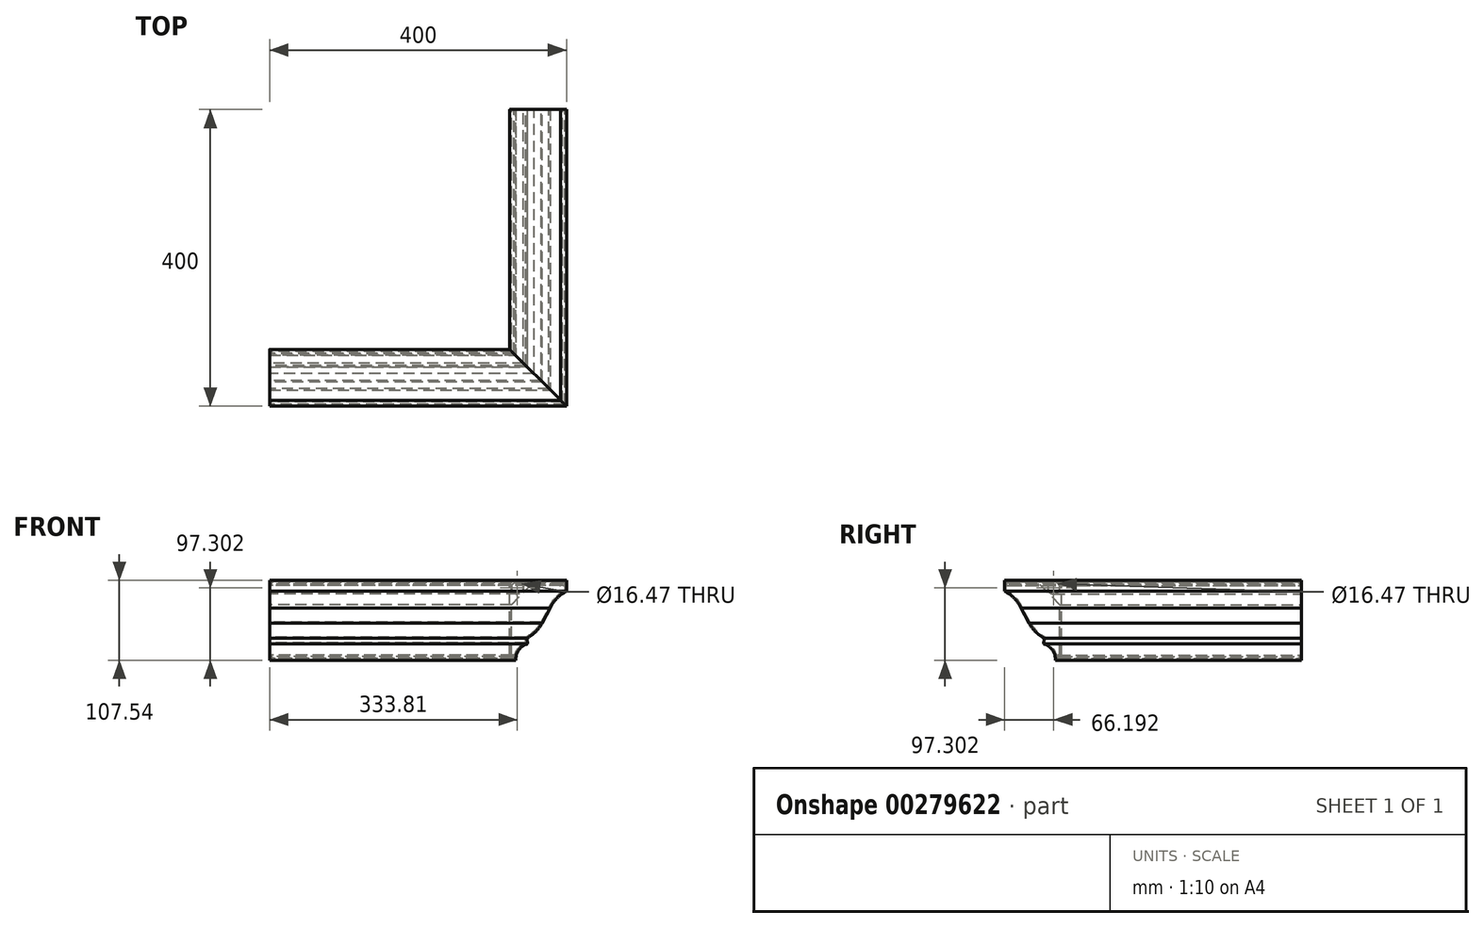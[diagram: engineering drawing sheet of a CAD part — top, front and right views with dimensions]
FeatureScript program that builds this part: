
annotation { "Feature Type Name" : "Feature", "Feature Type Description" : "" }
export const myFeature = defineFeature(function(context is Context, id is Id, definition is map)
    precondition{}
    {
        {
            var Q0;
            Q0=qCreatedBy(makeId("Front.planeOp"),FACE);
            var sketch = newSketch(context, id + "F0", { "sketchPlane" : qUnion([Q0])});
            skLineSegment(sketch, "E0", {"start": v(8.47, 2.23) * mm, "end": v(6.97, 0.18) * mm});
            skLineSegment(sketch, "E1", {"start": v(6.97, 0.18) * mm, "end": v(6.8, 0.14) * mm});
            skLineSegment(sketch, "E2", {"start": v(8.76, 2.82) * mm, "end": v(8.46, 2.4) * mm});
            skLineSegment(sketch, "E3", {"start": v(8.47, 2.23) * mm, "end": v(8.46, 2.4) * mm});
            skLineSegment(sketch, "E4", {"start": v(6.8, 0.14) * mm, "end": v(6.51, -0.24) * mm});
            skArc(sketch, "E5", {"start": v(9.24, 2.3) * mm, "mid": v(8.8, 1.98) * mm, "end": v(8.49, 1.53) * mm});
            skLineSegment(sketch, "E6", {"start": v(7.42, -0.15) * mm, "end": v(7.4, 0.13) * mm});
            skArc(sketch, "E7", {"start": v(7.42, -0.15) * mm, "mid": v(7.01, -0.43) * mm, "end": v(6.88, -0.9) * mm});
            skArc(sketch, "E8", {"start": v(7.4, 0.13) * mm, "mid": v(7.8, 0.42) * mm, "end": v(8.11, 0.82) * mm});
            skLineSegment(sketch, "E9", {"start": v(8.11, 0.82) * mm, "end": v(8.49, 1.53) * mm});
            skLineSegment(sketch, "E10", {"start": v(6.51, -0.9) * mm, "end": v(6.51, -0.24) * mm});
            skLineSegment(sketch, "E11", {"start": v(9.24, 2.82) * mm, "end": v(9.24, 2.3) * mm});
            skLineSegment(sketch, "E12", {"start": v(8.76, 2.82) * mm, "end": v(9.24, 2.82) * mm});
            skLineSegment(sketch, "E13", {"start": v(6.51, -0.9) * mm, "end": v(6.88, -0.9) * mm});
            skSolve(sketch);
        }
        {
            var Q0;
            Q0=makeQuery(id+"F0.imprint","IMPRINT",FACE,{"disambiguationData":[TD([[makeQuery(id+"F0.imprint","IMPRINT",EDGE,{"derivedFrom":sQuery(id+"F0.wireOp",EDGE,"E0")}),1.0]])]});
            extrude(context, id + "F1", {"entities" : qUnion([Q0]), "depth" : 0.1 * mm});
        }
        {
            var Q0;
            Q0=makeQuery(id+"F1.opExtrude","SWEPT_BODY",BODY,{"disambiguationData":[OSD([sQuery(id+"F0.wireOp",EDGE,"E0"),sQuery(id+"F0.wireOp",EDGE,"E1"),sQuery(id+"F0.wireOp",EDGE,"E2"),sQuery(id+"F0.wireOp",EDGE,"E3"),sQuery(id+"F0.wireOp",EDGE,"E4"),sQuery(id+"F0.wireOp",EDGE,"E5"),sQuery(id+"F0.wireOp",EDGE,"E6"),sQuery(id+"F0.wireOp",EDGE,"E7"),sQuery(id+"F0.wireOp",EDGE,"E8"),sQuery(id+"F0.wireOp",EDGE,"E9"),sQuery(id+"F0.wireOp",EDGE,"E10"),sQuery(id+"F0.wireOp",EDGE,"E11"),sQuery(id+"F0.wireOp",EDGE,"E12"),sQuery(id+"F0.wireOp",EDGE,"E13")])]});
            var Q1;
            Q1=makeQuery(id+"F1.opExtrude","CAP_VERTEX",VERTEX,{"disambiguationData":[OSD([sQuery(id+"F0.wireOp",EDGE,"E10"),sQuery(id+"F0.wireOp",EDGE,"E13")])],"isStart":false});
            transform(context, id + "F2", {"entities" : qUnion([Q0]), "transformType" : TransformType.SCALE_UNIFORMLY, "scale" : 28.87, "scalePoint" : qUnion([Q1]), "makeCopy" : false});
        }
        {
            var Q0;
            Q0=makeQuery(id+"F1.opExtrude","CAP_EDGE",EDGE,{"disambiguationData":[OSD([sQuery(id+"F0.wireOp",EDGE,"E0")])],"isStart":false});
            cPoint(context, id + "F3", {"entities" : qUnion([Q0]), "parameter" : 0.5});
        }
        {
            var Q0;
            Q0=makeQuery(id+"F1.opExtrude","SWEPT_BODY",BODY,{"disambiguationData":[OSD([sQuery(id+"F0.wireOp",EDGE,"E0"),sQuery(id+"F0.wireOp",EDGE,"E1"),sQuery(id+"F0.wireOp",EDGE,"E2"),sQuery(id+"F0.wireOp",EDGE,"E3"),sQuery(id+"F0.wireOp",EDGE,"E4"),sQuery(id+"F0.wireOp",EDGE,"E5"),sQuery(id+"F0.wireOp",EDGE,"E6"),sQuery(id+"F0.wireOp",EDGE,"E7"),sQuery(id+"F0.wireOp",EDGE,"E8"),sQuery(id+"F0.wireOp",EDGE,"E9"),sQuery(id+"F0.wireOp",EDGE,"E10"),sQuery(id+"F0.wireOp",EDGE,"E11"),sQuery(id+"F0.wireOp",EDGE,"E12"),sQuery(id+"F0.wireOp",EDGE,"E13")])]});
            var Q1;
            Q1 = qCreatedBy(id + "F3" ,VERTEX);
            var Q2;
            Q2=qCreatedBy(makeId("Origin.pointOp"),VERTEX);
            transform(context, id + "F4", {"entities" : qUnion([Q0]), "transformType" : TransformType.TRANSLATION_ENTITY, "oppositeDirectionEntity" : false, "transformLine" : qUnion([Q1, Q2]), "makeCopy" : false});
        }
        {
            var Q0;
            Q0=makeQuery(id+"F1.opExtrude","CAP_FACE",FACE,{"disambiguationData":[OSD([sQuery(id+"F0.wireOp",EDGE,"E0"),sQuery(id+"F0.wireOp",EDGE,"E1"),sQuery(id+"F0.wireOp",EDGE,"E2"),sQuery(id+"F0.wireOp",EDGE,"E3"),sQuery(id+"F0.wireOp",EDGE,"E4"),sQuery(id+"F0.wireOp",EDGE,"E5"),sQuery(id+"F0.wireOp",EDGE,"E6"),sQuery(id+"F0.wireOp",EDGE,"E7"),sQuery(id+"F0.wireOp",EDGE,"E8"),sQuery(id+"F0.wireOp",EDGE,"E9"),sQuery(id+"F0.wireOp",EDGE,"E10"),sQuery(id+"F0.wireOp",EDGE,"E11"),sQuery(id+"F0.wireOp",EDGE,"E12"),sQuery(id+"F0.wireOp",EDGE,"E13")])],"isStart":false});
            var sketch = newSketch(context, id + "F5", { "sketchPlane" : qUnion([Q0])});
            skArc(sketch, "E14.0", {"start": v(43.92, 31.78) * mm, "mid": v(30.94, 22.54) * mm, "end": v(22.09, 9.3) * mm});
            skLineSegment(sketch, "E15.0", {"start": v(11.27, -11.11) * mm, "end": v(22.09, 9.3) * mm});
            skArc(sketch, "E16.0", {"start": v(-9.07, -31.13) * mm, "mid": v(2.44, -22.49) * mm, "end": v(11.27, -11.11) * mm});
            skLineSegment(sketch, "E17.0", {"start": v(-8.82, -39.14) * mm, "end": v(-9.07, -31.13) * mm});
            skArc(sketch, "E18.0", {"start": v(-8.82, -39.14) * mm, "mid": v(-20.56, -47.27) * mm, "end": v(-24.46, -61.01) * mm});
            skLineSegment(sketch, "E19.0", {"start": v(43.92, 46.53) * mm, "end": v(43.92, 31.78) * mm});
            skLineSegment(sketch, "E20.0", {"start": v(-32.5, -61.01) * mm, "end": v(-24.46, -61.01) * mm});
            skLineSegment(sketch, "E21.0", {"start": v(35.92, 46.53) * mm, "end": v(43.92, 46.53) * mm});
            skLineSegment(sketch, "E22.0", {"start": v(-30.5, -59.01) * mm, "end": v(-26.5, -59.01) * mm});
            skArc(sketch, "E22.1", {"start": v(-10.87, -37.67) * mm, "mid": v(-22.03, -45.9) * mm, "end": v(-26.5, -59.01) * mm});
            skLineSegment(sketch, "E22.2", {"start": v(-10.87, -37.67) * mm, "end": v(-11.1, -29.96) * mm});
            skArc(sketch, "E22.3", {"start": v(-11.1, -29.96) * mm, "mid": v(0.6, -21.5) * mm, "end": v(9.52, -10.14) * mm});
            skLineSegment(sketch, "E22.4", {"start": v(37.92, 44.53) * mm, "end": v(41.92, 44.53) * mm});
            skLineSegment(sketch, "E22.5", {"start": v(41.92, 44.53) * mm, "end": v(41.92, 33.03) * mm});
            skArc(sketch, "E22.6", {"start": v(41.92, 33.03) * mm, "mid": v(29.1, 23.5) * mm, "end": v(20.28, 10.16) * mm});
            skLineSegment(sketch, "E22.7", {"start": v(9.52, -10.14) * mm, "end": v(20.28, 10.16) * mm});
            skLineSegment(sketch, "E23", {"start": v(35.92, 46.53) * mm, "end": v(35.92, 41.53) * mm});
            skLineSegment(sketch, "E24", {"start": v(37.92, 44.53) * mm, "end": v(37.92, 41.53) * mm});
            skPoint(sketch, "E25.orphan", {"position": v(29.94, 46.53) * mm});
            skLineSegment(sketch, "E26", {"start": v(35.92, 41.53) * mm, "end": v(37.92, 41.53) * mm});
            skLineSegment(sketch, "E27", {"start": v(-32.5, -61.01) * mm, "end": v(-32.5, -56.01) * mm});
            skLineSegment(sketch, "E28.0", {"start": v(-30.5, -59.01) * mm, "end": v(-30.5, -56.01) * mm});
            skPoint(sketch, "E29.orphan", {"position": v(-34.89, -61.01) * mm});
            skLineSegment(sketch, "E30", {"start": v(-32.5, -56.01) * mm, "end": v(-30.5, -56.01) * mm});
            skSolve(sketch);
        }
        {
            var Q0;
            Q0=makeQuery(id+"F5.imprint","IMPRINT",FACE,{"disambiguationData":[TD([[makeQuery(id+"F5.imprint","IMPRINT",EDGE,{"derivedFrom":sQuery(id+"F5.wireOp",EDGE,"E14.0")}),-1.0]])]});
            extrude(context, id + "F6", {"entities" : qUnion([Q0]), "operationType" : NewBodyOperationType.ADD, "depth" : 400 * mm});
        }
        {
            var Q0;
            Q0=makeQuery(id+"F6.opExtrude","CAP_FACE",FACE,{"disambiguationData":[OSD([sQuery(id+"F5.wireOp",EDGE,"E14.0"),sQuery(id+"F5.wireOp",EDGE,"E15.0"),sQuery(id+"F5.wireOp",EDGE,"E16.0"),sQuery(id+"F5.wireOp",EDGE,"E17.0"),sQuery(id+"F5.wireOp",EDGE,"E18.0"),sQuery(id+"F5.wireOp",EDGE,"E19.0"),sQuery(id+"F5.wireOp",EDGE,"E20.0"),sQuery(id+"F5.wireOp",EDGE,"E21.0"),sQuery(id+"F5.wireOp",EDGE,"E22.0"),sQuery(id+"F5.wireOp",EDGE,"E22.1"),sQuery(id+"F5.wireOp",EDGE,"E22.2"),sQuery(id+"F5.wireOp",EDGE,"E22.3"),sQuery(id+"F5.wireOp",EDGE,"E22.4"),sQuery(id+"F5.wireOp",EDGE,"E22.5"),sQuery(id+"F5.wireOp",EDGE,"E22.6"),sQuery(id+"F5.wireOp",EDGE,"E22.7"),sQuery(id+"F5.wireOp",EDGE,"E23"),sQuery(id+"F5.wireOp",EDGE,"E24"),sQuery(id+"F5.wireOp",EDGE,"E26"),sQuery(id+"F5.wireOp",EDGE,"E27"),sQuery(id+"F5.wireOp",EDGE,"E28.0"),sQuery(id+"F5.wireOp",EDGE,"E30")])],"isStart":false});
            cPlane(context, id + "F7", {"entities" : qUnion([Q0]), "cplaneType" : CPlaneType.OFFSET, "offset" : 25 * mm, "width" : 150 * mm, "height" : 150 * mm});
        }
        {
            var Q0;
            Q0=qCreatedBy(id+"F7.planeOp",FACE);
            var sketch = newSketch(context, id + "F8", { "sketchPlane" : qUnion([Q0])});
            skLineSegment(sketch, "E31.0.0", {"start": v(43.92, 46.53) * mm, "end": v(35.92, 46.53) * mm});
            skLineSegment(sketch, "E31.0.1", {"start": v(35.92, 46.53) * mm, "end": v(35.92, 41.53) * mm});
            skLineSegment(sketch, "E31.0.2", {"start": v(35.92, 41.53) * mm, "end": v(37.92, 41.53) * mm});
            skLineSegment(sketch, "E31.0.3", {"start": v(37.92, 41.53) * mm, "end": v(37.92, 44.53) * mm});
            skLineSegment(sketch, "E31.0.4", {"start": v(37.92, 44.53) * mm, "end": v(41.92, 44.53) * mm});
            skLineSegment(sketch, "E31.0.5", {"start": v(41.92, 44.53) * mm, "end": v(41.92, 33.03) * mm});
            skArc(sketch, "E31.0.6", {"start": v(41.92, 33.03) * mm, "mid": v(29.1, 23.5) * mm, "end": v(20.28, 10.16) * mm});
            skLineSegment(sketch, "E31.0.7", {"start": v(20.28, 10.16) * mm, "end": v(9.52, -10.14) * mm});
            skArc(sketch, "E31.0.8", {"start": v(9.52, -10.14) * mm, "mid": v(0.6, -21.5) * mm, "end": v(-11.1, -29.96) * mm});
            skLineSegment(sketch, "E31.0.9", {"start": v(-11.1, -29.96) * mm, "end": v(-10.87, -37.67) * mm});
            skArc(sketch, "E31.0.10", {"start": v(-10.87, -37.67) * mm, "mid": v(-22.03, -45.9) * mm, "end": v(-26.5, -59.01) * mm});
            skLineSegment(sketch, "E31.0.11", {"start": v(-26.5, -59.01) * mm, "end": v(-30.5, -59.01) * mm});
            skLineSegment(sketch, "E31.0.12", {"start": v(-30.5, -59.01) * mm, "end": v(-30.5, -56.01) * mm});
            skLineSegment(sketch, "E31.0.13", {"start": v(-30.5, -56.01) * mm, "end": v(-32.5, -56.01) * mm});
            skLineSegment(sketch, "E31.0.14", {"start": v(-32.5, -56.01) * mm, "end": v(-32.5, -61.01) * mm});
            skLineSegment(sketch, "E31.0.15", {"start": v(-32.5, -61.01) * mm, "end": v(-24.46, -61.01) * mm});
            skArc(sketch, "E31.0.16", {"start": v(-24.46, -61.01) * mm, "mid": v(-20.56, -47.27) * mm, "end": v(-8.82, -39.14) * mm});
            skLineSegment(sketch, "E31.0.17", {"start": v(-8.82, -39.14) * mm, "end": v(-9.07, -31.13) * mm});
            skArc(sketch, "E31.0.18", {"start": v(-9.07, -31.13) * mm, "mid": v(2.44, -22.49) * mm, "end": v(11.27, -11.11) * mm});
            skLineSegment(sketch, "E31.0.19", {"start": v(11.27, -11.11) * mm, "end": v(22.09, 9.3) * mm});
            skArc(sketch, "E31.0.20", {"start": v(22.09, 9.3) * mm, "mid": v(30.94, 22.54) * mm, "end": v(43.92, 31.78) * mm});
            skLineSegment(sketch, "E31.0.21", {"start": v(43.92, 31.78) * mm, "end": v(43.92, 46.53) * mm});
            skSolve(sketch);
        }
        {
            var Q0;
            Q0=makeQuery(id+"F8.imprint","IMPRINT",FACE,{"disambiguationData":[TD([[makeQuery(id+"F8.imprint","IMPRINT",EDGE,{"derivedFrom":sQuery(id+"F8.wireOp",EDGE,"E31.0.0")}),1.0]])]});
            extrude(context, id + "F9", {"entities" : qUnion([Q0]), "depth" : 400 * mm});
        }
        {
            var Q0;
            Q0=makeQuery(id+"F9.opExtrude","CAP_FACE",FACE,{"disambiguationData":[OSD([sQuery(id+"F8.wireOp",EDGE,"E31.0.0"),sQuery(id+"F8.wireOp",EDGE,"E31.0.1"),sQuery(id+"F8.wireOp",EDGE,"E31.0.2"),sQuery(id+"F8.wireOp",EDGE,"E31.0.3"),sQuery(id+"F8.wireOp",EDGE,"E31.0.4"),sQuery(id+"F8.wireOp",EDGE,"E31.0.5"),sQuery(id+"F8.wireOp",EDGE,"E31.0.6"),sQuery(id+"F8.wireOp",EDGE,"E31.0.7"),sQuery(id+"F8.wireOp",EDGE,"E31.0.8"),sQuery(id+"F8.wireOp",EDGE,"E31.0.9"),sQuery(id+"F8.wireOp",EDGE,"E31.0.10"),sQuery(id+"F8.wireOp",EDGE,"E31.0.11"),sQuery(id+"F8.wireOp",EDGE,"E31.0.12"),sQuery(id+"F8.wireOp",EDGE,"E31.0.13"),sQuery(id+"F8.wireOp",EDGE,"E31.0.14"),sQuery(id+"F8.wireOp",EDGE,"E31.0.15"),sQuery(id+"F8.wireOp",EDGE,"E31.0.16"),sQuery(id+"F8.wireOp",EDGE,"E31.0.17"),sQuery(id+"F8.wireOp",EDGE,"E31.0.18"),sQuery(id+"F8.wireOp",EDGE,"E31.0.19"),sQuery(id+"F8.wireOp",EDGE,"E31.0.20"),sQuery(id+"F8.wireOp",EDGE,"E31.0.21")])],"isStart":true});
            cPlane(context, id + "F10", {"entities" : qUnion([Q0]), "cplaneType" : CPlaneType.OFFSET, "offset" : 0 * mm, "width" : 150 * mm, "height" : 150 * mm});
        }
        {
            var Q0;
            Q0=qCreatedBy(id+"F10.planeOp",FACE);
            var sketch = newSketch(context, id + "F11", { "sketchPlane" : qUnion([Q0])});
            skLineSegment(sketch, "E32.0", {"start": v(-32, 46.53) * mm, "end": v(29.5, 46.53) * mm});
            skLineSegment(sketch, "E33.0", {"start": v(32.5, 43.53) * mm, "end": v(32.5, -56.01) * mm});
            skLineSegment(sketch, "E34.0", {"start": v(30.5, 44.53) * mm, "end": v(30.5, 43.03) * mm});
            skLineSegment(sketch, "E34.1", {"start": v(-31.65, 44.53) * mm, "end": v(-0.24, 44.53) * mm});
            skLineSegment(sketch, "E35", {"start": v(-35.92, 41.53) * mm, "end": v(-34.82, 44.55) * mm});
            skLineSegment(sketch, "E36", {"start": v(-37.92, 41.53) * mm, "end": v(-38.3, 43.19) * mm});
            skLineSegment(sketch, "E37", {"start": v(-35.92, 41.53) * mm, "end": v(-37.92, 41.53) * mm});
            skLineSegment(sketch, "E38.0", {"start": v(-37.92, 44.53) * mm, "end": v(-41.92, 44.53) * mm});
            skPoint(sketch, "E39.orphan", {"position": v(-38.61, 44.53) * mm});
            skLineSegment(sketch, "E40", {"start": v(-37.92, 41.53) * mm, "end": v(-41.42, 41.53) * mm, "construction": true});
            skLineSegment(sketch, "E41.0", {"start": v(-35.57, 39.53) * mm, "end": v(-37.92, 39.53) * mm});
            skLineSegment(sketch, "E42.0", {"start": v(-34.16, 40.51) * mm, "end": v(-33.06, 43.54) * mm});
            skPoint(sketch, "E43.orphan", {"position": v(-35.92, 44.53) * mm});
            skPoint(sketch, "E44.orphan", {"position": v(-35.92, 46.53) * mm});
            skArc(sketch, "E45", {"start": v(-38.3, 43.19) * mm, "mid": v(-41.33, 42.11) * mm, "end": v(-39.42, 39.53) * mm});
            skPoint(sketch, "E46.MirrorCS.end.orphan", {"position": v(-41.42, 41.53) * mm});
            skPoint(sketch, "E47.visualSharp", {"position": v(-32.7, 44.53) * mm});
            skArc(sketch, "E47.filletArc", {"start": v(-31.65, 44.53) * mm, "mid": v(-32.51, 44.26) * mm, "end": v(-33.06, 43.54) * mm});
            skPoint(sketch, "E48.visualSharp", {"position": v(-34.1, 46.53) * mm});
            skArc(sketch, "E48.filletArc", {"start": v(-32, 46.53) * mm, "mid": v(-33.72, 45.98) * mm, "end": v(-34.82, 44.55) * mm});
            skPoint(sketch, "E49.visualSharp", {"position": v(-34.52, 39.53) * mm});
            skArc(sketch, "E49.filletArc", {"start": v(-35.57, 39.53) * mm, "mid": v(-34.71, 39.8) * mm, "end": v(-34.16, 40.51) * mm});
            skPoint(sketch, "E50.visualSharp", {"position": v(30.5, 44.53) * mm});
            skPoint(sketch, "E51.visualSharp", {"position": v(32.5, 46.53) * mm});
            skArc(sketch, "E51.filletArc", {"start": v(32.5, 43.53) * mm, "mid": v(31.63, 45.65) * mm, "end": v(29.5, 46.53) * mm});
            skLineSegment(sketch, "E52", {"start": v(-37.92, 39.53) * mm, "end": v(-39.42, 39.53) * mm});
            skPoint(sketch, "E53.start.orphan", {"position": v(-38.3, 39.87) * mm});
            skLineSegment(sketch, "E54", {"start": v(30.5, -56.01) * mm, "end": v(29, -56.01) * mm, "construction": true});
            skArc(sketch, "E55", {"start": v(29.05, -54.01) * mm, "mid": v(27.08, -56.58) * mm, "end": v(30.12, -57.67) * mm});
            skLineSegment(sketch, "E56", {"start": v(30.5, -56.01) * mm, "end": v(30.12, -57.67) * mm});
            skLineSegment(sketch, "E57.0", {"start": v(30.5, -59.01) * mm, "end": v(30.5, -56.01) * mm});
            skLineSegment(sketch, "E58.0", {"start": v(30.5, -56.01) * mm, "end": v(32.5, -56.01) * mm});
            skLineSegment(sketch, "E59", {"start": v(29.05, -54.01) * mm, "end": v(29.97, -54.04) * mm});
            skPoint(sketch, "E60.visualSharp", {"position": v(30.5, -54.05) * mm});
            skArc(sketch, "E60.filletArc", {"start": v(29.97, -54.04) * mm, "mid": v(30.35, -53.89) * mm, "end": v(30.5, -53.51) * mm});
            skLineSegment(sketch, "E61", {"start": v(-0.24, 44.53) * mm, "end": v(30.5, 13.78) * mm});
            skLineSegment(sketch, "E62", {"start": v(15.13, 29.15) * mm, "end": v(22.27, 36.3) * mm, "construction": true});
            skCircle(sketch, "E63", {"center": v(22.27, 36.3) * mm, "radius": 8.23 * mm});
            skLineSegment(sketch, "E64.trimOffspring", {"start": v(29, 44.53) * mm, "end": v(30.5, 44.53) * mm});
            skLineSegment(sketch, "E65.trimOffspring", {"start": v(30.5, 13.78) * mm, "end": v(30.5, -53.51) * mm});
            skSolve(sketch);
        }
        {
            var Q0;
            Q0=makeQuery(id+"F11.imprint","IMPRINT",FACE,{"disambiguationData":[TD([[makeQuery(id+"F11.imprint","IMPRINT",EDGE,{"derivedFrom":sQuery(id+"F11.wireOp",EDGE,"E32.0")}),-1.0]])]});
            extrude(context, id + "F12", {"entities" : qUnion([Q0]), "oppositeDirection" : true, "depth" : 400 * mm});
        }
        {
            var Q0;
            Q0=makeQuery(id+"F12.opExtrude","SWEPT_FACE",FACE,{"disambiguationData":[OSD([sQuery(id+"F11.wireOp",EDGE,"E32.0")])]});
            cPlane(context, id + "F13", {"entities" : qUnion([Q0]), "cplaneType" : CPlaneType.OFFSET, "offset" : 0 * mm, "width" : 150 * mm, "height" : 150 * mm});
        }
        {
            var Q0;
            Q0=qCreatedBy(id+"F13.planeOp",FACE);
            var sketch = newSketch(context, id + "F14", { "sketchPlane" : qUnion([Q0])});
            skLineSegment(sketch, "E66.0", {"start": v(43.92, -825) * mm, "end": v(35.92, -825) * mm});
            skLineSegment(sketch, "E67.0", {"start": v(35.92, -825) * mm, "end": v(34.82, -825) * mm});
            skLineSegment(sketch, "E68.0", {"start": v(32, -825) * mm, "end": v(34.82, -825) * mm});
            skLineSegment(sketch, "E69.0", {"start": v(32, -825) * mm, "end": v(-29.5, -825) * mm});
            skLineSegment(sketch, "E70.0", {"start": v(-32.5, -825) * mm, "end": v(-29.5, -825) * mm});
            skLineSegment(sketch, "E71.0", {"start": v(-32.5, -825) * mm, "end": v(-32.5, -425) * mm});
            skLineSegment(sketch, "E72", {"start": v(43.92, -825) * mm, "end": v(-32.5, -748.57) * mm});
            skSolve(sketch);
        }
        {
            var Q0;
            Q0=makeQuery(id+"F1.opExtrude","SWEPT_BODY",BODY,{"disambiguationData":[OSD([sQuery(id+"F0.wireOp",EDGE,"E0"),sQuery(id+"F0.wireOp",EDGE,"E1"),sQuery(id+"F0.wireOp",EDGE,"E2"),sQuery(id+"F0.wireOp",EDGE,"E3"),sQuery(id+"F0.wireOp",EDGE,"E4"),sQuery(id+"F0.wireOp",EDGE,"E5"),sQuery(id+"F0.wireOp",EDGE,"E6"),sQuery(id+"F0.wireOp",EDGE,"E7"),sQuery(id+"F0.wireOp",EDGE,"E8"),sQuery(id+"F0.wireOp",EDGE,"E9"),sQuery(id+"F0.wireOp",EDGE,"E10"),sQuery(id+"F0.wireOp",EDGE,"E11"),sQuery(id+"F0.wireOp",EDGE,"E12"),sQuery(id+"F0.wireOp",EDGE,"E13")])]});
            deleteBodies(context, id + "F15", {"entities" : qUnion([Q0])});
        }
        {
            var Q0;
            Q0=makeQuery(id+"F14.imprint","IMPRINT",FACE,{"disambiguationData":[TD([[makeQuery(id+"F14.imprint","IMPRINT",EDGE,{"derivedFrom":sQuery(id+"F14.wireOp",EDGE,"E66.0")}),-1.0]])]});
            var Q1;
            Q1=makeQuery(id+"F9.opExtrude","SWEPT_FACE",FACE,{"disambiguationData":[OSD([sQuery(id+"F8.wireOp",EDGE,"E31.0.15")])]});
            var Q2;
            Q2=makeQuery(id+"F9.opExtrude","SWEPT_BODY",BODY,{"disambiguationData":[OSD([sQuery(id+"F8.wireOp",EDGE,"E31.0.0"),sQuery(id+"F8.wireOp",EDGE,"E31.0.1"),sQuery(id+"F8.wireOp",EDGE,"E31.0.2"),sQuery(id+"F8.wireOp",EDGE,"E31.0.3"),sQuery(id+"F8.wireOp",EDGE,"E31.0.4"),sQuery(id+"F8.wireOp",EDGE,"E31.0.5"),sQuery(id+"F8.wireOp",EDGE,"E31.0.6"),sQuery(id+"F8.wireOp",EDGE,"E31.0.7"),sQuery(id+"F8.wireOp",EDGE,"E31.0.8"),sQuery(id+"F8.wireOp",EDGE,"E31.0.9"),sQuery(id+"F8.wireOp",EDGE,"E31.0.10"),sQuery(id+"F8.wireOp",EDGE,"E31.0.11"),sQuery(id+"F8.wireOp",EDGE,"E31.0.12"),sQuery(id+"F8.wireOp",EDGE,"E31.0.13"),sQuery(id+"F8.wireOp",EDGE,"E31.0.14"),sQuery(id+"F8.wireOp",EDGE,"E31.0.15"),sQuery(id+"F8.wireOp",EDGE,"E31.0.16"),sQuery(id+"F8.wireOp",EDGE,"E31.0.17"),sQuery(id+"F8.wireOp",EDGE,"E31.0.18"),sQuery(id+"F8.wireOp",EDGE,"E31.0.19"),sQuery(id+"F8.wireOp",EDGE,"E31.0.20"),sQuery(id+"F8.wireOp",EDGE,"E31.0.21")])]});
            extrude(context, id + "F16", {"entities" : qUnion([Q0, Q1]), "operationType" : NewBodyOperationType.REMOVE, "endBound" : BoundingType.THROUGH_ALL, "oppositeDirection" : true, "endBoundEntityBody" : qUnion([Q2]), "depth" : 25 * mm});
        }
        {
            var Q0;
            Q0=makeQuery(id+"F12.opExtrude","SWEPT_BODY",BODY,{"disambiguationData":[OSD([sQuery(id+"F11.wireOp",EDGE,"E32.0"),sQuery(id+"F11.wireOp",EDGE,"E33.0"),sQuery(id+"F11.wireOp",EDGE,"E34.1"),sQuery(id+"F11.wireOp",EDGE,"E35"),sQuery(id+"F11.wireOp",EDGE,"E36"),sQuery(id+"F11.wireOp",EDGE,"E37"),sQuery(id+"F11.wireOp",EDGE,"E41.0"),sQuery(id+"F11.wireOp",EDGE,"E42.0"),sQuery(id+"F11.wireOp",EDGE,"E45"),sQuery(id+"F11.wireOp",EDGE,"E47.filletArc"),sQuery(id+"F11.wireOp",EDGE,"E48.filletArc"),sQuery(id+"F11.wireOp",EDGE,"E49.filletArc"),sQuery(id+"F11.wireOp",EDGE,"E51.filletArc"),sQuery(id+"F11.wireOp",EDGE,"E52"),sQuery(id+"F11.wireOp",EDGE,"E55"),sQuery(id+"F11.wireOp",EDGE,"E56"),sQuery(id+"F11.wireOp",EDGE,"E58.0"),sQuery(id+"F11.wireOp",EDGE,"E59"),sQuery(id+"F11.wireOp",EDGE,"E60.filletArc"),sQuery(id+"F11.wireOp",EDGE,"E61"),sQuery(id+"F11.wireOp",EDGE,"E63"),sQuery(id+"F11.wireOp",EDGE,"E65.trimOffspring")])]});
            var Q1;
            Q1=makeQuery(id+"F9.opExtrude","SWEPT_BODY",BODY,{"disambiguationData":[OSD([sQuery(id+"F8.wireOp",EDGE,"E31.0.0"),sQuery(id+"F8.wireOp",EDGE,"E31.0.1"),sQuery(id+"F8.wireOp",EDGE,"E31.0.2"),sQuery(id+"F8.wireOp",EDGE,"E31.0.3"),sQuery(id+"F8.wireOp",EDGE,"E31.0.4"),sQuery(id+"F8.wireOp",EDGE,"E31.0.5"),sQuery(id+"F8.wireOp",EDGE,"E31.0.6"),sQuery(id+"F8.wireOp",EDGE,"E31.0.7"),sQuery(id+"F8.wireOp",EDGE,"E31.0.8"),sQuery(id+"F8.wireOp",EDGE,"E31.0.9"),sQuery(id+"F8.wireOp",EDGE,"E31.0.10"),sQuery(id+"F8.wireOp",EDGE,"E31.0.11"),sQuery(id+"F8.wireOp",EDGE,"E31.0.12"),sQuery(id+"F8.wireOp",EDGE,"E31.0.13"),sQuery(id+"F8.wireOp",EDGE,"E31.0.14"),sQuery(id+"F8.wireOp",EDGE,"E31.0.15"),sQuery(id+"F8.wireOp",EDGE,"E31.0.16"),sQuery(id+"F8.wireOp",EDGE,"E31.0.17"),sQuery(id+"F8.wireOp",EDGE,"E31.0.18"),sQuery(id+"F8.wireOp",EDGE,"E31.0.19"),sQuery(id+"F8.wireOp",EDGE,"E31.0.20"),sQuery(id+"F8.wireOp",EDGE,"E31.0.21")])]});
            var Q2;
            Q2=makeQuery(id+"F16.boolean.opBoolean","COPY",FACE,{"disambiguationData":[TD([makeQuery(id+"F12.opExtrude","SWEPT_FACE",FACE,{"disambiguationData":[OSD([sQuery(id+"F11.wireOp",EDGE,"E32.0")])]})])],"derivedFrom":makeQuery(id+"F16.opExtrude","SWEPT_FACE",FACE,{"disambiguationData":[OSD([sQuery(id+"F14.wireOp",EDGE,"E72")])]})});
            mirror(context, id + "F17", {"entities" : qUnion([Q0, Q1]), "mirrorPlane" : qUnion([Q2])});
        }
    });
